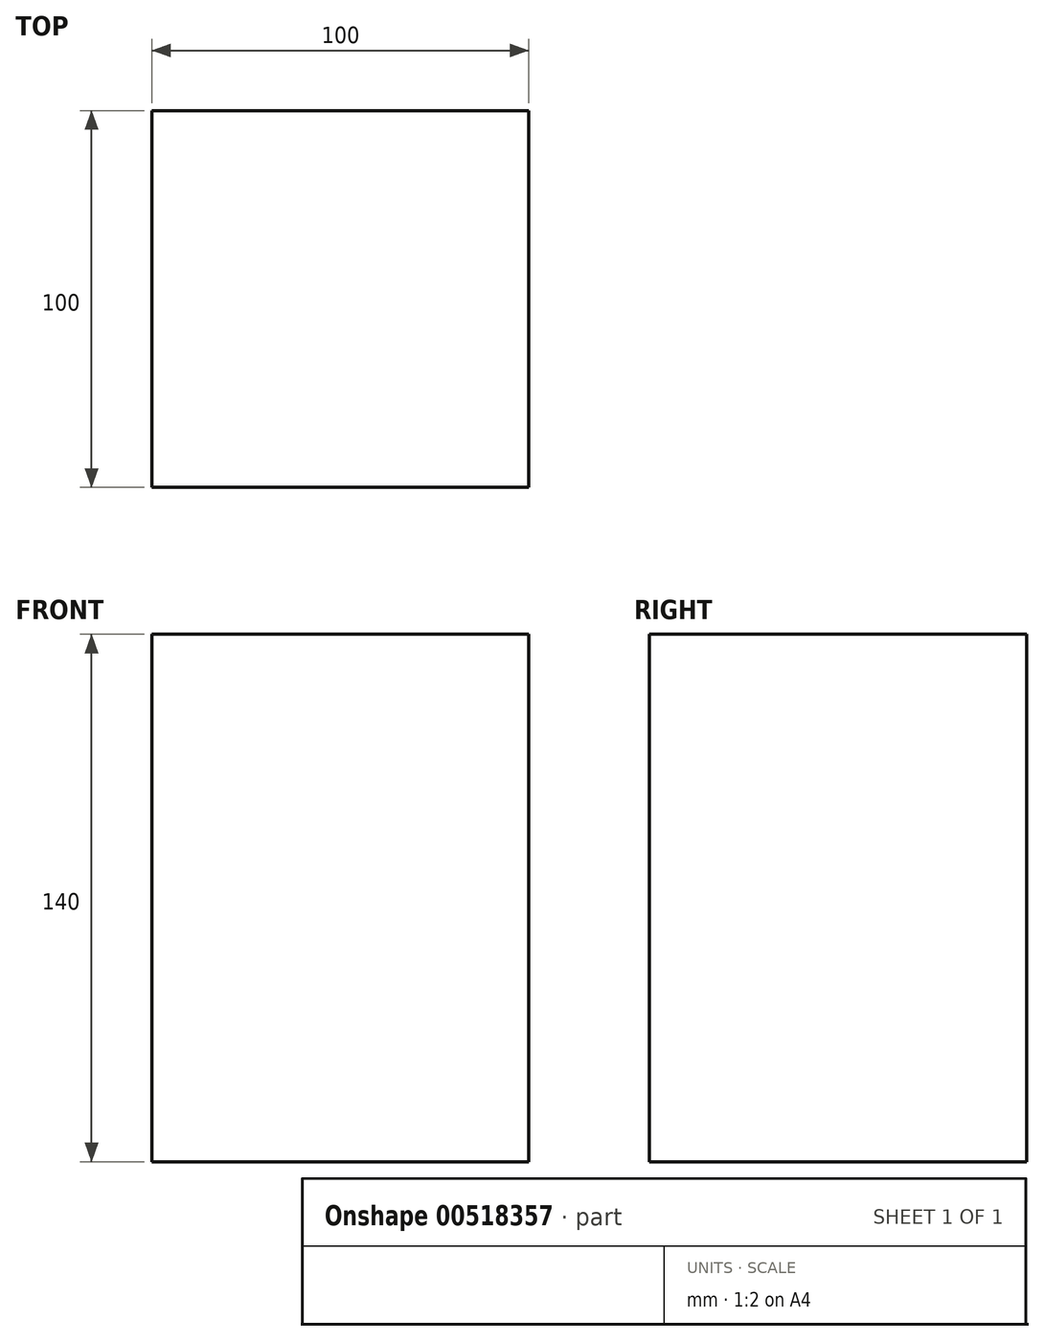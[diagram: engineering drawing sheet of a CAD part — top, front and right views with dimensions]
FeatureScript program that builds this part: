
annotation { "Feature Type Name" : "Feature", "Feature Type Description" : "" }
export const myFeature = defineFeature(function(context is Context, id is Id, definition is map)
    precondition{}
    {
        {
            var Q0;
            Q0=qCreatedBy(makeId("Top.planeOp"),FACE);
            var sketch = newSketch(context, id + "F0", { "sketchPlane" : qUnion([Q0])});
            skLineSegment(sketch, "E0.bottom", {"start": v(0, 0) * mm, "end": v(100, 0) * mm});
            skLineSegment(sketch, "E0.top", {"start": v(0, 100) * mm, "end": v(100, 100) * mm});
            skLineSegment(sketch, "E0.left", {"start": v(0, 0) * mm, "end": v(0, 100) * mm});
            skLineSegment(sketch, "E0.right", {"start": v(100, 0) * mm, "end": v(100, 100) * mm});
            skSolve(sketch);
        }
        {
            var Q0;
            Q0 = qSketchRegion(id + "F0", true);
            extrude(context, id + "F1", {"entities" : qUnion([Q0]), "depth" : 140 * mm, "offsetDistance" : 25 * mm});
        }
        {
            var Q0;
            Q0=makeQuery(id+"F1.opExtrude","CAP_FACE",FACE,{"disambiguationData":[OSD([sQuery(id+"F0.wireOp",EDGE,"E0.bottom"),sQuery(id+"F0.wireOp",EDGE,"E0.top"),sQuery(id+"F0.wireOp",EDGE,"E0.left"),sQuery(id+"F0.wireOp",EDGE,"E0.right")])],"isStart":false});
            var sketch = newSketch(context, id + "F2", { "sketchPlane" : qUnion([Q0])});
            skLineSegment(sketch, "E1", {"start": v(50, 100) * mm, "end": v(50, 0) * mm});
            skLineSegment(sketch, "E2", {"start": v(0, 50) * mm, "end": v(100, 50) * mm});
            skSolve(sketch);
        }
    });
